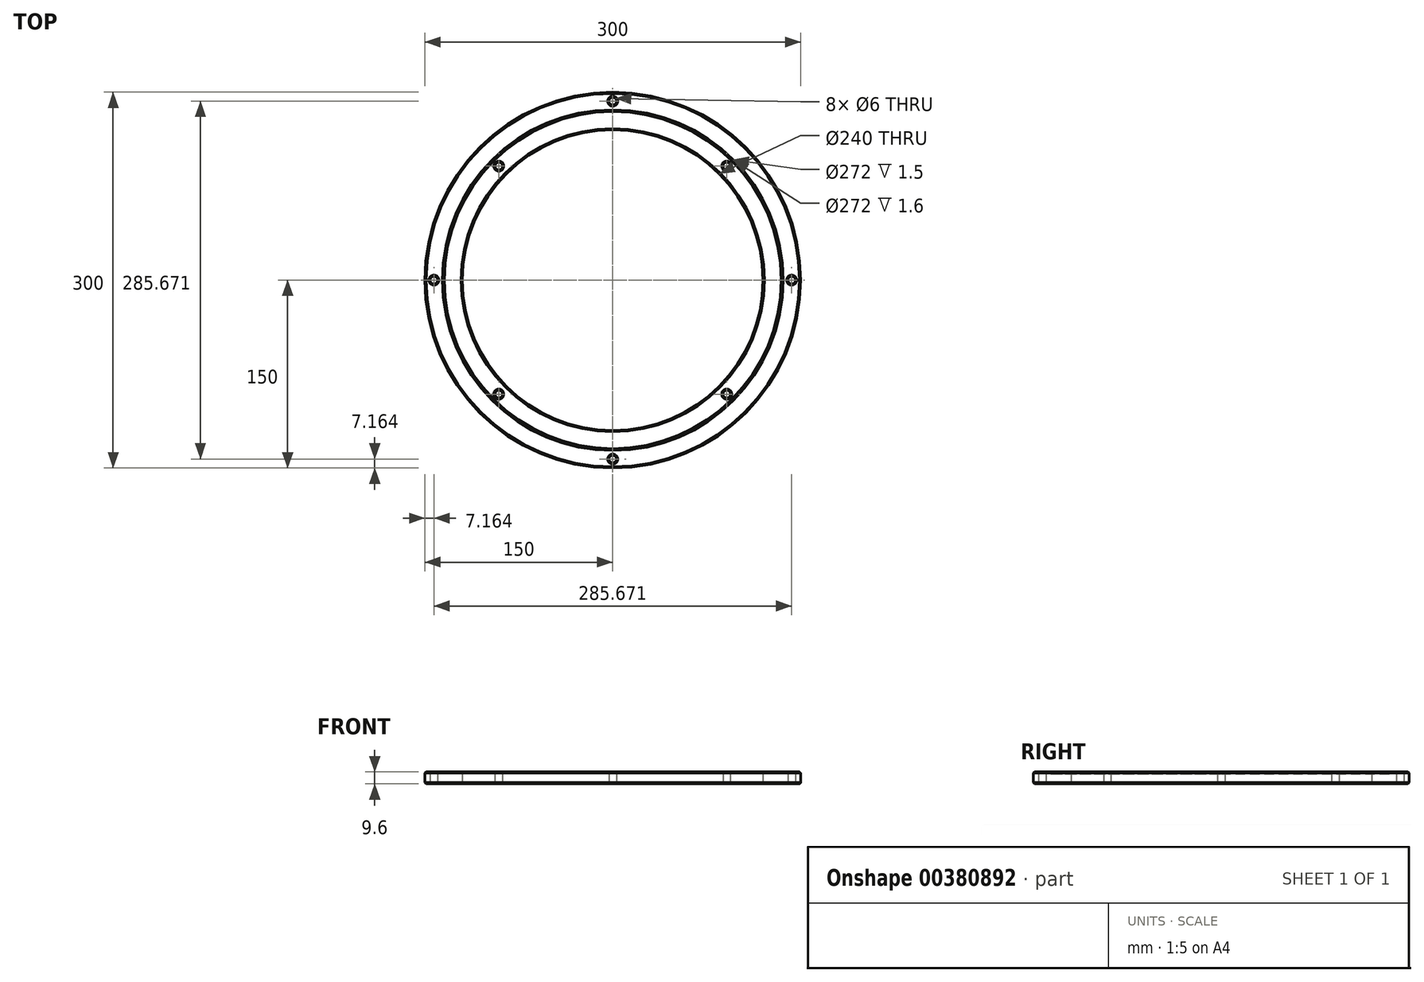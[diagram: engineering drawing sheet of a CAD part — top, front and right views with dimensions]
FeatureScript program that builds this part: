
annotation { "Feature Type Name" : "Feature", "Feature Type Description" : "" }
export const myFeature = defineFeature(function(context is Context, id is Id, definition is map)
    precondition{}
    {
        {
            var Q0;
            Q0=qCreatedBy(makeId("Top.planeOp"),FACE);
            var sketch = newSketch(context, id + "F0", { "sketchPlane" : qUnion([Q0])});
            skCircle(sketch, "E0", {"center": v(0, 0) * mm, "radius": 150 * mm});
            skCircle(sketch, "E1", {"center": v(0, 0) * mm, "radius": 120 * mm});
            skCircle(sketch, "E2", {"center": v(0, 0) * mm, "radius": 134.5 * mm});
            skCircle(sketch, "E3", {"center": v(0, 0) * mm, "radius": 136 * mm});
            skSolve(sketch);
        }
        {
            var Q0;
            Q0=makeQuery(id+"F0.imprint","IMPRINT",FACE,{"disambiguationData":[TD([[makeQuery(id+"F0.imprint","IMPRINT",EDGE,{"derivedFrom":sQuery(id+"F0.wireOp",EDGE,"E0")}),1.0]])]});
            var Q1;
            Q1=makeQuery(id+"F0.imprint","IMPRINT",FACE,{"disambiguationData":[TD([[makeQuery(id+"F0.imprint","IMPRINT",EDGE,{"derivedFrom":sQuery(id+"F0.wireOp",EDGE,"E1")}),-1.0]])]});
            var Q2;
            Q2=makeQuery(id+"F0.imprint","IMPRINT",FACE,{"disambiguationData":[TD([[makeQuery(id+"F0.imprint","IMPRINT",EDGE,{"derivedFrom":sQuery(id+"F0.wireOp",EDGE,"E2")}),-1.0]])]});
            extrude(context, id + "F1", {"entities" : qUnion([Q0, Q1, Q2]), "depth" : 9.6 * mm});
        }
        {
            var Q0;
            Q0=makeQuery(id+"F1.opExtrude","CAP_EDGE",EDGE,{"disambiguationData":[OSD([sQuery(id+"F0.wireOp",EDGE,"E1")])],"isStart":false});
            var Q1;
            Q1=makeQuery(id+"F1.opExtrude","CAP_EDGE",EDGE,{"disambiguationData":[OSD([sQuery(id+"F0.wireOp",EDGE,"E0")])],"isStart":false});
            var Q2;
            Q2=makeQuery(id+"F1.opExtrude","CAP_FACE",FACE,{"disambiguationData":[OSD([sQuery(id+"F0.wireOp",EDGE,"E0"),sQuery(id+"F0.wireOp",EDGE,"E1")])],"isStart":true});
            chamfer(context, id + "F2", {"entities" : qUnion([Q0, Q1, Q2]), "width" : 1 * mm, "tangentPropagation" : true});
        }
        {
            var Q0;
            Q0=makeQuery(id+"F0.imprint","IMPRINT",FACE,{"disambiguationData":[TD([[makeQuery(id+"F0.imprint","IMPRINT",EDGE,{"derivedFrom":sQuery(id+"F0.wireOp",EDGE,"E2")}),-1.0]])]});
            extrude(context, id + "F3", {"entities" : qUnion([Q0]), "operationType" : NewBodyOperationType.REMOVE, "depth" : 1.5 * mm});
        }
        {
            var Q0;
            Q0=makeQuery(id+"F0.imprint","IMPRINT",FACE,{"disambiguationData":[TD([[makeQuery(id+"F0.imprint","IMPRINT",EDGE,{"derivedFrom":sQuery(id+"F0.wireOp",EDGE,"E2")}),-1.0]])]});
            extrude(context, id + "F4", {"entities" : qUnion([Q0]), "operationType" : NewBodyOperationType.REMOVE, "depth" : 25 * mm, "hasSecondDirection" : true, "secondDirectionOppositeDirection" : false, "secondDirectionDepth" : 8 * mm});
        }
        {
            var Q0;
            Q0=qCreatedBy(makeId("Top.planeOp"),FACE);
            var sketch = newSketch(context, id + "F5", { "sketchPlane" : qUnion([Q0])});
            skLineSegment(sketch, "E4.bottom", {"start": v(91, -91) * mm, "end": v(-91, -91) * mm});
            skLineSegment(sketch, "E4.top", {"start": v(91, 91) * mm, "end": v(-91, 91) * mm});
            skLineSegment(sketch, "E4.left", {"start": v(91, -91) * mm, "end": v(91, 91) * mm});
            skLineSegment(sketch, "E4.right", {"start": v(-91, -91) * mm, "end": v(-91, 91) * mm});
            skPoint(sketch, "E4.middle", {"position": v(0, 0) * mm});
            skCircle(sketch, "E5", {"center": v(-91, 91) * mm, "radius": 3 * mm});
            skCircle(sketch, "E6", {"center": v(91, 91) * mm, "radius": 3 * mm});
            skCircle(sketch, "E7", {"center": v(91, -91) * mm, "radius": 3 * mm});
            skCircle(sketch, "E8", {"center": v(-91, -91) * mm, "radius": 3 * mm});
            skLineSegment(sketch, "E9.bottom", {"start": v(101, -101) * mm, "end": v(-101, -101) * mm});
            skLineSegment(sketch, "E9.top", {"start": v(101, 101) * mm, "end": v(-101, 101) * mm});
            skLineSegment(sketch, "E9.left", {"start": v(101, -101) * mm, "end": v(101, 101) * mm});
            skLineSegment(sketch, "E9.right", {"start": v(-101, -101) * mm, "end": v(-101, 101) * mm});
            skCircle(sketch, "E10", {"center": v(-142.84, 0) * mm, "radius": 3 * mm});
            skCircle(sketch, "E11", {"center": v(0, 142.84) * mm, "radius": 3 * mm});
            skCircle(sketch, "E12", {"center": v(142.84, 0) * mm, "radius": 3 * mm});
            skCircle(sketch, "E13", {"center": v(0, -142.84) * mm, "radius": 3 * mm});
            skSolve(sketch);
        }
        {
            var Q0;
            {var subQ0=sQuery(id+"F5.wireOp",EDGE,"E4.right");var subQ1=sQuery(id+"F5.wireOp",EDGE,"E4.bottom");var subQ2=makeQuery(id+"F5.imprint","INTERSECT",VERTEX,{"derivedFrom":[subQ1,subQ0]});Q0=makeQuery(id+"F5.imprint","IMPRINT",FACE,{"disambiguationData":[TD([[makeQuery(id+"F5.imprint","IMPRINT",EDGE,{"disambiguationData":[TD([[subQ2,1.0]])],"derivedFrom":subQ1}),1.0]])]});}
            var Q1;
            {var subQ0=sQuery(id+"F5.wireOp",EDGE,"E4.right");var subQ1=sQuery(id+"F5.wireOp",EDGE,"E4.bottom");var subQ2=makeQuery(id+"F5.imprint","INTERSECT",VERTEX,{"derivedFrom":[subQ1,subQ0]});Q1=makeQuery(id+"F5.imprint","IMPRINT",FACE,{"disambiguationData":[TD([[makeQuery(id+"F5.imprint","IMPRINT",EDGE,{"disambiguationData":[TD([[subQ2,1.0]])],"derivedFrom":subQ1}),-1.0]])]});}
            var Q2;
            {var subQ0=sQuery(id+"F5.wireOp",EDGE,"E4.right");var subQ1=sQuery(id+"F5.wireOp",EDGE,"E4.top");var subQ2=makeQuery(id+"F5.imprint","INTERSECT",VERTEX,{"derivedFrom":[subQ1,subQ0]});Q2=makeQuery(id+"F5.imprint","IMPRINT",FACE,{"disambiguationData":[TD([[makeQuery(id+"F5.imprint","IMPRINT",EDGE,{"disambiguationData":[TD([[subQ2,1.0]])],"derivedFrom":subQ1}),1.0]])]});}
            var Q3;
            {var subQ0=sQuery(id+"F5.wireOp",EDGE,"E4.right");var subQ1=sQuery(id+"F5.wireOp",EDGE,"E4.top");var subQ2=makeQuery(id+"F5.imprint","INTERSECT",VERTEX,{"derivedFrom":[subQ1,subQ0]});Q3=makeQuery(id+"F5.imprint","IMPRINT",FACE,{"disambiguationData":[TD([[makeQuery(id+"F5.imprint","IMPRINT",EDGE,{"disambiguationData":[TD([[subQ2,1.0]])],"derivedFrom":subQ1}),-1.0]])]});}
            var Q4;
            {var subQ0=sQuery(id+"F5.wireOp",EDGE,"E4.left");var subQ1=sQuery(id+"F5.wireOp",EDGE,"E4.top");var subQ2=makeQuery(id+"F5.imprint","INTERSECT",VERTEX,{"derivedFrom":[subQ1,subQ0]});Q4=makeQuery(id+"F5.imprint","IMPRINT",FACE,{"disambiguationData":[TD([[makeQuery(id+"F5.imprint","IMPRINT",EDGE,{"disambiguationData":[TD([[subQ2,-1.0]])],"derivedFrom":subQ1}),-1.0]])]});}
            var Q5;
            {var subQ0=sQuery(id+"F5.wireOp",EDGE,"E4.left");var subQ1=sQuery(id+"F5.wireOp",EDGE,"E4.top");var subQ2=makeQuery(id+"F5.imprint","INTERSECT",VERTEX,{"derivedFrom":[subQ1,subQ0]});Q5=makeQuery(id+"F5.imprint","IMPRINT",FACE,{"disambiguationData":[TD([[makeQuery(id+"F5.imprint","IMPRINT",EDGE,{"disambiguationData":[TD([[subQ2,-1.0]])],"derivedFrom":subQ1}),1.0]])]});}
            var Q6;
            {var subQ0=sQuery(id+"F5.wireOp",EDGE,"E4.left");var subQ1=sQuery(id+"F5.wireOp",EDGE,"E4.bottom");var subQ2=makeQuery(id+"F5.imprint","INTERSECT",VERTEX,{"derivedFrom":[subQ1,subQ0]});Q6=makeQuery(id+"F5.imprint","IMPRINT",FACE,{"disambiguationData":[TD([[makeQuery(id+"F5.imprint","IMPRINT",EDGE,{"disambiguationData":[TD([[subQ2,-1.0]])],"derivedFrom":subQ1}),1.0]])]});}
            var Q7;
            {var subQ0=sQuery(id+"F5.wireOp",EDGE,"E4.left");var subQ1=sQuery(id+"F5.wireOp",EDGE,"E4.bottom");var subQ2=makeQuery(id+"F5.imprint","INTERSECT",VERTEX,{"derivedFrom":[subQ1,subQ0]});Q7=makeQuery(id+"F5.imprint","IMPRINT",FACE,{"disambiguationData":[TD([[makeQuery(id+"F5.imprint","IMPRINT",EDGE,{"disambiguationData":[TD([[subQ2,-1.0]])],"derivedFrom":subQ1}),-1.0]])]});}
            var Q8;
            Q8=makeQuery(id+"F5.imprint","IMPRINT",FACE,{"disambiguationData":[TD([[makeQuery(id+"F5.imprint","IMPRINT",EDGE,{"derivedFrom":sQuery(id+"F5.wireOp",EDGE,"E13")}),1.0]])]});
            var Q9;
            Q9=makeQuery(id+"F5.imprint","IMPRINT",FACE,{"disambiguationData":[TD([[makeQuery(id+"F5.imprint","IMPRINT",EDGE,{"derivedFrom":sQuery(id+"F5.wireOp",EDGE,"E12")}),1.0]])]});
            var Q10;
            Q10=makeQuery(id+"F5.imprint","IMPRINT",FACE,{"disambiguationData":[TD([[makeQuery(id+"F5.imprint","IMPRINT",EDGE,{"derivedFrom":sQuery(id+"F5.wireOp",EDGE,"E11")}),1.0]])]});
            var Q11;
            Q11=makeQuery(id+"F5.imprint","IMPRINT",FACE,{"disambiguationData":[TD([[makeQuery(id+"F5.imprint","IMPRINT",EDGE,{"derivedFrom":sQuery(id+"F5.wireOp",EDGE,"E10")}),1.0]])]});
            extrude(context, id + "F6", {"entities" : qUnion([Q0, Q1, Q2, Q3, Q4, Q5, Q6, Q7, Q8, Q9, Q10, Q11]), "operationType" : NewBodyOperationType.REMOVE, "depth" : 25 * mm});
        }
        {
            var Q0;
            {var subQ0=sQuery(id+"F0.wireOp",EDGE,"E1");Q0=makeQuery(id+"F6.boolean.opBoolean","INTERSECT",EDGE,{"derivedFrom":[makeQuery(id+"F4.boolean.opBoolean","SPLIT",FACE,{"disambiguationData":[TD([makeQuery(id+"F4.opExtrude","SWEPT_FACE",FACE,{"disambiguationData":[OSD([sQuery(id+"F0.wireOp",EDGE,"E2")])]})])],"derivedFrom":makeQuery(id+"F1.opExtrude","CAP_FACE",FACE,{"disambiguationData":[OSD([sQuery(id+"F0.wireOp",EDGE,"E0"),subQ0])],"isStart":false})}),makeQuery(id+"F6.opExtrude","SWEPT_FACE",FACE,{"disambiguationData":[OSD([sQuery(id+"F5.wireOp",EDGE,"E8")])]})]});}
            var Q1;
            {var subQ0=sQuery(id+"F0.wireOp",EDGE,"E1");Q1=makeQuery(id+"F6.boolean.opBoolean","INTERSECT",EDGE,{"derivedFrom":[makeQuery(id+"F4.boolean.opBoolean","SPLIT",FACE,{"disambiguationData":[TD([makeQuery(id+"F4.opExtrude","SWEPT_FACE",FACE,{"disambiguationData":[OSD([sQuery(id+"F0.wireOp",EDGE,"E2")])]})])],"derivedFrom":makeQuery(id+"F1.opExtrude","CAP_FACE",FACE,{"disambiguationData":[OSD([sQuery(id+"F0.wireOp",EDGE,"E0"),subQ0])],"isStart":false})}),makeQuery(id+"F6.opExtrude","SWEPT_FACE",FACE,{"disambiguationData":[OSD([sQuery(id+"F5.wireOp",EDGE,"E7")])]})]});}
            var Q2;
            {var subQ0=sQuery(id+"F0.wireOp",EDGE,"E1");Q2=makeQuery(id+"F6.boolean.opBoolean","INTERSECT",EDGE,{"derivedFrom":[makeQuery(id+"F4.boolean.opBoolean","SPLIT",FACE,{"disambiguationData":[TD([makeQuery(id+"F4.opExtrude","SWEPT_FACE",FACE,{"disambiguationData":[OSD([sQuery(id+"F0.wireOp",EDGE,"E2")])]})])],"derivedFrom":makeQuery(id+"F1.opExtrude","CAP_FACE",FACE,{"disambiguationData":[OSD([sQuery(id+"F0.wireOp",EDGE,"E0"),subQ0])],"isStart":false})}),makeQuery(id+"F6.opExtrude","SWEPT_FACE",FACE,{"disambiguationData":[OSD([sQuery(id+"F5.wireOp",EDGE,"E5")])]})]});}
            var Q3;
            {var subQ0=sQuery(id+"F0.wireOp",EDGE,"E1");Q3=makeQuery(id+"F6.boolean.opBoolean","INTERSECT",EDGE,{"derivedFrom":[makeQuery(id+"F4.boolean.opBoolean","SPLIT",FACE,{"disambiguationData":[TD([makeQuery(id+"F4.opExtrude","SWEPT_FACE",FACE,{"disambiguationData":[OSD([sQuery(id+"F0.wireOp",EDGE,"E2")])]})])],"derivedFrom":makeQuery(id+"F1.opExtrude","CAP_FACE",FACE,{"disambiguationData":[OSD([sQuery(id+"F0.wireOp",EDGE,"E0"),subQ0])],"isStart":false})}),makeQuery(id+"F6.opExtrude","SWEPT_FACE",FACE,{"disambiguationData":[OSD([sQuery(id+"F5.wireOp",EDGE,"E6")])]})]});}
            var Q4;
            Q4=makeQuery(id+"F6.boolean.opBoolean","COPY",EDGE,{"derivedFrom":makeQuery(id+"F6.opExtrude","CAP_EDGE",EDGE,{"disambiguationData":[OSD([sQuery(id+"F5.wireOp",EDGE,"E6")])],"isStart":true})});
            var Q5;
            Q5=makeQuery(id+"F6.boolean.opBoolean","COPY",EDGE,{"derivedFrom":makeQuery(id+"F6.opExtrude","CAP_EDGE",EDGE,{"disambiguationData":[OSD([sQuery(id+"F5.wireOp",EDGE,"E5")])],"isStart":true})});
            var Q6;
            Q6=makeQuery(id+"F6.boolean.opBoolean","COPY",EDGE,{"derivedFrom":makeQuery(id+"F6.opExtrude","CAP_EDGE",EDGE,{"disambiguationData":[OSD([sQuery(id+"F5.wireOp",EDGE,"E7")])],"isStart":true})});
            var Q7;
            Q7=makeQuery(id+"F6.boolean.opBoolean","COPY",EDGE,{"derivedFrom":makeQuery(id+"F6.opExtrude","CAP_EDGE",EDGE,{"disambiguationData":[OSD([sQuery(id+"F5.wireOp",EDGE,"E8")])],"isStart":true})});
            var Q8;
            Q8=makeQuery(id+"F6.boolean.opBoolean","COPY",EDGE,{"derivedFrom":makeQuery(id+"F6.opExtrude","CAP_EDGE",EDGE,{"disambiguationData":[OSD([sQuery(id+"F5.wireOp",EDGE,"E11")])],"isStart":true})});
            var Q9;
            {var subQ0=sQuery(id+"F0.wireOp",EDGE,"E0");Q9=makeQuery(id+"F6.boolean.opBoolean","INTERSECT",EDGE,{"derivedFrom":[makeQuery(id+"F4.boolean.opBoolean","SPLIT",FACE,{"disambiguationData":[TD([makeQuery(id+"F4.opExtrude","SWEPT_FACE",FACE,{"disambiguationData":[OSD([sQuery(id+"F0.wireOp",EDGE,"E3")])]})])],"derivedFrom":makeQuery(id+"F1.opExtrude","CAP_FACE",FACE,{"disambiguationData":[OSD([subQ0,sQuery(id+"F0.wireOp",EDGE,"E1")])],"isStart":false})}),makeQuery(id+"F6.opExtrude","SWEPT_FACE",FACE,{"disambiguationData":[OSD([sQuery(id+"F5.wireOp",EDGE,"E11")])]})]});}
            var Q10;
            {var subQ0=sQuery(id+"F0.wireOp",EDGE,"E0");Q10=makeQuery(id+"F6.boolean.opBoolean","INTERSECT",EDGE,{"derivedFrom":[makeQuery(id+"F4.boolean.opBoolean","SPLIT",FACE,{"disambiguationData":[TD([makeQuery(id+"F4.opExtrude","SWEPT_FACE",FACE,{"disambiguationData":[OSD([sQuery(id+"F0.wireOp",EDGE,"E3")])]})])],"derivedFrom":makeQuery(id+"F1.opExtrude","CAP_FACE",FACE,{"disambiguationData":[OSD([subQ0,sQuery(id+"F0.wireOp",EDGE,"E1")])],"isStart":false})}),makeQuery(id+"F6.opExtrude","SWEPT_FACE",FACE,{"disambiguationData":[OSD([sQuery(id+"F5.wireOp",EDGE,"E12")])]})]});}
            var Q11;
            Q11=makeQuery(id+"F6.boolean.opBoolean","COPY",EDGE,{"derivedFrom":makeQuery(id+"F6.opExtrude","CAP_EDGE",EDGE,{"disambiguationData":[OSD([sQuery(id+"F5.wireOp",EDGE,"E12")])],"isStart":true})});
            var Q12;
            {var subQ0=sQuery(id+"F0.wireOp",EDGE,"E0");Q12=makeQuery(id+"F6.boolean.opBoolean","INTERSECT",EDGE,{"derivedFrom":[makeQuery(id+"F4.boolean.opBoolean","SPLIT",FACE,{"disambiguationData":[TD([makeQuery(id+"F4.opExtrude","SWEPT_FACE",FACE,{"disambiguationData":[OSD([sQuery(id+"F0.wireOp",EDGE,"E3")])]})])],"derivedFrom":makeQuery(id+"F1.opExtrude","CAP_FACE",FACE,{"disambiguationData":[OSD([subQ0,sQuery(id+"F0.wireOp",EDGE,"E1")])],"isStart":false})}),makeQuery(id+"F6.opExtrude","SWEPT_FACE",FACE,{"disambiguationData":[OSD([sQuery(id+"F5.wireOp",EDGE,"E13")])]})]});}
            var Q13;
            Q13=makeQuery(id+"F6.boolean.opBoolean","COPY",EDGE,{"derivedFrom":makeQuery(id+"F6.opExtrude","CAP_EDGE",EDGE,{"disambiguationData":[OSD([sQuery(id+"F5.wireOp",EDGE,"E13")])],"isStart":true})});
            var Q14;
            {var subQ0=sQuery(id+"F0.wireOp",EDGE,"E0");Q14=makeQuery(id+"F6.boolean.opBoolean","INTERSECT",EDGE,{"derivedFrom":[makeQuery(id+"F4.boolean.opBoolean","SPLIT",FACE,{"disambiguationData":[TD([makeQuery(id+"F4.opExtrude","SWEPT_FACE",FACE,{"disambiguationData":[OSD([sQuery(id+"F0.wireOp",EDGE,"E3")])]})])],"derivedFrom":makeQuery(id+"F1.opExtrude","CAP_FACE",FACE,{"disambiguationData":[OSD([subQ0,sQuery(id+"F0.wireOp",EDGE,"E1")])],"isStart":false})}),makeQuery(id+"F6.opExtrude","SWEPT_FACE",FACE,{"disambiguationData":[OSD([sQuery(id+"F5.wireOp",EDGE,"E10")])]})]});}
            var Q15;
            Q15=makeQuery(id+"F6.boolean.opBoolean","COPY",EDGE,{"derivedFrom":makeQuery(id+"F6.opExtrude","CAP_EDGE",EDGE,{"disambiguationData":[OSD([sQuery(id+"F5.wireOp",EDGE,"E10")])],"isStart":true})});
            chamfer(context, id + "F7", {"entities" : qUnion([Q0, Q1, Q2, Q3, Q4, Q5, Q6, Q7, Q8, Q9, Q10, Q11, Q12, Q13, Q14, Q15]), "width" : 1 * mm, "tangentPropagation" : true});
        }
    });
